# Revit family: Zylinderschraube mit Innensechskant DIN EN ISO 4762
name_source: partatom
category: HLS-Bauteile
revit_build: Autodesk Revit 2017 (Build: 20190507_1515(x64)
units: mm (PartAtom-declared; Revit-internal decimal feet)

## family parameters
Arbeitsebenenbasiert = Ja
Beim Laden mit Abzugskörper schneiden = Nein
Bemaßung runder Anschluss = Durchmesser verwenden
Gemeinsam genutzt = Ja
Immer vertikal = Nein
Raumberechnungspunkt = Nein
Teiletyp = Normal

## types (5) — shared parameters
Antrieb = Inbus
Fabrikat = MEFA
Firma = MEFA Befestigungs- und Montagesysteme GmbH
Form Kopf = Zylinderkopf
Kurztext1 = Zylinderschraube EN ISO 4762
Material = Stahl
Mengeneinheit = St
Oberflaeche = galvanisch verzinkt
Vorgabe-Ansicht = 1219 mm

## per-type parameters (varying)
| type | Antriebsgröße | Artikelnummer | D Kopf | Durchmesser Kopf | EAN | Gewicht | Gewicht pro Bauteil | Gewinde | H Kopf | Kurztext2 | L | Länge | S | d2 | vpe |
| Zylinderschraube m. Innen6kant M 8x 20 | 6 | 3443205 | 7 mm  [stored 0.0229659 ft] | 13 mm | 4250928438362 | 0.01 kg | 0.01 kg | M8 | 8 mm  [stored 0.0262467 ft] | M8 x 20 mm Inbus 6 gvz | 20 mm  [stored 0.0656168 ft] | 20 mm  [stored 0.0656168 ft] | 6 mm  [stored 0.019685 ft] | 3 mm  [stored 0.00984252 ft] | 100 St |
| Zylinderschraube m. Innen6kant M10x 25 | 8 | 3444252 | 8 mm  [stored 0.0262467 ft] | 16 mm | 4250928438386 | 0.03 kg | 0.03 kg | M10 | 10 mm  [stored 0.0328084 ft] | M10 x 25 mm Inbus 8 gvz | 25 mm  [stored 0.082021 ft] | 25 mm  [stored 0.082021 ft] | 8 mm  [stored 0.0262467 ft] | 4 mm  [stored 0.0131234 ft] | 100 St |
| Zylinderschraube m. Innen6kant M12x 25 | 10 | 3445259 | 9 mm  [stored 0.0295276 ft] | 18 mm | 4250928438454 | 0.04 kg | 0.04 kg | M12 | 12 mm  [stored 0.0393701 ft] | M12 x 25 mm Inbus 10 gvz | 25 mm  [stored 0.082021 ft] | 25 mm  [stored 0.082021 ft] | 10 mm  [stored 0.0328084 ft] | 5 mm  [stored 0.0164042 ft] | 100 St |
| Zylinderschraube m. Innen6kant M 8x 16 | 6 | 3443167 | 7 mm  [stored 0.0229659 ft] | 13 mm | 4250928438355 | 0.01 kg | 0.01 kg | M8 | 8 mm  [stored 0.0262467 ft] | M8 x 16 mm Inbus 6 gvz | 16 mm  [stored 0.0524934 ft] | 16 mm  [stored 0.0524934 ft] | 6 mm  [stored 0.019685 ft] | 3 mm  [stored 0.00984252 ft] | 200 St |
| Zylinderschraube m. Innen6kant M10x 20 | 8 | 3444200 | 8 mm  [stored 0.0262467 ft] | 16 mm | 4250928438379 | 0.02 kg | 0.02 kg | M10 | 10 mm  [stored 0.0328084 ft] | M10 x 20 mm Inbus 8 gvz | 20 mm  [stored 0.0656168 ft] | 20 mm  [stored 0.0656168 ft] | 8 mm  [stored 0.0262467 ft] | 4 mm  [stored 0.0131234 ft] | 100 St |

note: [stored X ft] marks values corroborated as IEEE doubles in the binary element streams (Revit-internal decimal feet)
